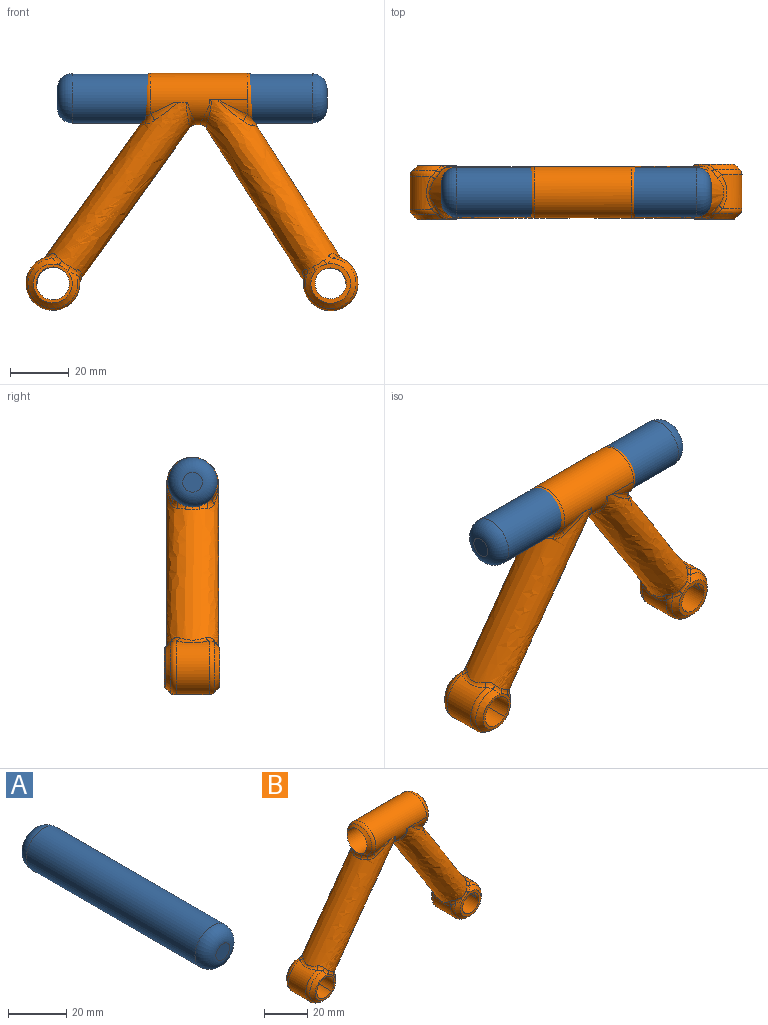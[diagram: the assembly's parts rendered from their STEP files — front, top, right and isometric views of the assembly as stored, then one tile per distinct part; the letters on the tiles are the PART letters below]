
ASSEMBLY  parts=2 mates=1
PART A: 5 faces, bbox 16.9x92.2x16.9 mm
  f0: cylinder r=8.44mm len=82.04mm, axis (0,1,0), area 4351.7mm2, adj f3,f4
  f1: plane 6.72x6.72mm, normal (0,-1,0), area 35.5mm2, adj f4
  f2: plane 6.72x6.72mm, normal (0,1,0), area 35.5mm2, adj f3
  f3: torus R=3.36mm, axis (0,-1,0), area 330.7mm2, adj f0,f2
  f4: torus R=3.36mm, axis (0,-1,0), area 330.7mm2, adj f0,f1
PART B: 77 faces, bbox 115.2x35.7x82.8 mm
  f0: bspline ~61.06x60.5mm, area -3132mm2, adj f1,f14,f15,f16,f17,f18,f61,f62
  f1: bspline ~3.72x3.66mm, area 5.3mm2, adj f0,f2,f14,f75
  f2: cone r=6.64mm half-angle=45deg, axis (0,1,0), area 103.2mm2, adj f1,f3,f13,f15
  f3: plane 13.37x13.37mm, normal (0,1,0), area 39.1mm2, adj f2,f4,f12,f14
  f4: cylinder r=5.63mm len=18.46mm, axis (0,1,0), area 294.9mm2, adj f3,f5,f9,f10,f11,f12
  f5: plane 13.4x13.4mm, normal (0,-1,0), area 39.1mm2, adj f4,f6,f12,f71
  f6: cone r=9.18mm half-angle=45deg, axis (0,-1,0), area 102.3mm2, adj f5,f7,f70,f72
  f7: torus R=6.64mm, axis (0,1,0), area 86.6mm2, adj f6,f8,f73,f76
  f8: cylinder r=9.18mm len=18.37mm, axis (0,1,0), area 458.9mm2, adj f7,f13,f17,f74
  f9: bspline ~62.14x61.9mm, area 2.3mm2, adj f4,f10,f12
  f10: plane 14.44x0.21mm, normal (0,0,1), area 2.9mm2, adj f4,f9,f11,f12
  f11: bspline ~62.14x61.9mm, area 2.3mm2, adj f4,f10,f12
  f12: cylinder r=5.54mm len=18.46mm, axis (0,-1,0), area 357.5mm2, adj f3,f4,f5,f9,f10,f11
  f13: torus R=6.64mm, axis (0,-1,0), area 86.9mm2, adj f2,f8,f16,f75
  f14: bspline ~3.96x3.44mm, area 5.7mm2, adj f0,f1,f3,f15
  f15: bspline ~4.19x3.14mm, area 5.4mm2, adj f0,f2,f14,f16
  f16: bspline ~3.67x3.62mm, area 6.2mm2, adj f0,f13,f15,f17
  f17: bspline ~12.35x3.69mm, area 19.5mm2, adj f0,f8,f16,f76
  f18: plane 4.62x0.29mm, normal (0,0,-1), area 0.4mm2, adj f0,f19,f61,f69
  f19: cylinder r=8.79mm len=33.15mm, axis (-1,0,0), area 1126.3mm2, adj f18,f20,f55,f56,f57,f58,f59,f60
  f20: torus R=6.25mm, axis (-1,0,0), area 78.1mm2, adj f19,f21,f62,f66
  f21: cone r=8.79mm half-angle=45deg, axis (1,0,0), area 82mm2, adj f20,f22,f54,f63,f65
  f22: cylinder r=6.45mm len=40.34mm, axis (1,0,0), area 1635mm2, adj f21,f23,f53,f54
  f23: plane 6.63x0.95mm, normal (-1,0,0), area 0.2mm2, adj f22,f24,f53
  f24: bspline ~3.25x2.13mm, area 3.5mm2, adj f23,f25,f28,f52
  f25: bspline ~5.66x3.16mm, area 14.1mm2, adj f24,f26,f28,f53
  f26: bspline ~4.31x4.23mm, area 10.1mm2, adj f25,f27,f28,f58
  f27: bspline ~11.26x8.45mm, area 18.7mm2, adj f26,f28,f59,f60
  f28: bspline ~61.2x56.79mm, area 3044.4mm2, adj f24,f25,f26,f27,f29,f42,f43,f44
  f29: bspline ~3.79x3.75mm, area 6.1mm2, adj f28,f30,f42,f51
  f30: torus R=6.78mm, axis (0,-1,0), area 87.2mm2, adj f29,f31,f41,f48
  f31: cylinder r=9.32mm len=18.64mm, axis (0,1,0), area 475.5mm2, adj f30,f32,f42,f47
  f32: torus R=6.78mm, axis (0,1,0), area 89.2mm2, adj f31,f33,f43,f45
  f33: cone r=9.32mm half-angle=45deg, axis (0,-1,0), area 107.2mm2, adj f32,f34,f44
  f34: plane 13.56x13.56mm, normal (0,-1,0), area 55.2mm2, adj f33,f35,f40
  f35: cylinder r=5.24mm len=18.79mm, axis (0,-1,0), area 378.4mm2, adj f34,f36,f37,f38,f39,f40
  f36: plane 13.7x13.7mm, normal (0,1,0), area 55.2mm2, adj f35,f40,f41,f50
  f37: bspline ~62.76x57.82mm, area 1.9mm2, adj f35,f38,f40
  f38: plane 14.79x0.21mm, normal (0,0,1), area 3mm2, adj f35,f37,f39,f40
  f39: bspline ~62.76x57.82mm, area 1.9mm2, adj f35,f38,f40
  f40: cylinder r=5.31mm len=18.79mm, axis (0,1,0), area 249mm2, adj f34,f35,f36,f37,f38,f39
  f41: cone r=6.78mm half-angle=45deg, axis (0,1,0), area 103.3mm2, adj f30,f36,f49,f51
  f42: bspline ~13.05x4.05mm, area 19.8mm2, adj f28,f29,f31,f43
  f43: bspline ~4.16x4.01mm, area 6.8mm2, adj f28,f32,f42,f44
  f44: bspline ~9.08x6.53mm, area 16.6mm2, adj f28,f33,f43,f45
  f45: bspline ~4.62x4.09mm, area 6.7mm2, adj f28,f32,f44,f47
  f46: bspline ~4.41x4.4mm, area 10.1mm2, adj f28,f52,f57,f58
  f47: bspline ~13.31x3.55mm, area 18.9mm2, adj f28,f31,f45,f48
  f48: bspline ~3.8x3.54mm, area 5.9mm2, adj f28,f30,f47,f49
  f49: bspline ~4.16x3.84mm, area 5mm2, adj f28,f41,f48,f50
  f50: bspline ~5.84x4.65mm, area 6.1mm2, adj f28,f36,f49,f51
  f51: bspline ~3.57x2.77mm, area 5.1mm2, adj f28,f29,f41,f50
  f52: bspline ~5.12x3.16mm, area 14.1mm2, adj f24,f28,f46,f53
  f53: cone r=6.25mm half-angle=45deg, axis (-1,0,0), area 100.3mm2, adj f22,f23,f25,f52,f58
  f54: plane 6.74x1.06mm, normal (1,0,0), area 0.2mm2, adj f21,f22,f64
  f55: bspline ~17.63x10.2mm, area 47.5mm2, adj f19,f28,f56,f60
  f56: plane 3.34x0.15mm, normal (0,0,-1), area 0.2mm2, adj f19,f28,f55,f57
  f57: bspline ~11.08x8.22mm, area 18.7mm2, adj f19,f28,f46,f56
  f58: torus R=6.25mm, axis (1,0,0), area 80.1mm2, adj f19,f26,f46,f53,f59
  f59: cylinder r=8.79mm len=9.72mm, axis (-1,0,0), area 26.1mm2, adj f19,f27,f58
  f60: plane 3.33x0.15mm, normal (0,0,-1), area 0.2mm2, adj f19,f27,f28,f55
  f61: bspline ~10.72x7.52mm, area 17.1mm2, adj f0,f18,f19,f62
  f62: bspline ~4.28x4.13mm, area 9.4mm2, adj f0,f20,f61,f63
  f63: bspline ~4.88x3.22mm, area 10mm2, adj f0,f21,f62,f64
  f64: bspline ~4.84x3.16mm, area 13.9mm2, adj f0,f54,f63,f65
  f65: bspline ~4.48x3.2mm, area 10mm2, adj f0,f21,f64,f66
  f66: bspline ~3.97x3.89mm, area 9.4mm2, adj f0,f20,f65,f67
  f67: bspline ~10.64x7.48mm, area 17.1mm2, adj f0,f19,f66,f68
  f68: plane 4.62x0.29mm, normal (0,0,-1), area 0.4mm2, adj f0,f19,f67,f69
  f69: bspline ~17.54x8.92mm, area 44.4mm2, adj f0,f18,f19,f68
  f70: bspline ~3.91x2.88mm, area 5.2mm2, adj f0,f6,f71,f76
  f71: bspline ~4.32x3.67mm, area 5.8mm2, adj f0,f5,f70,f72
  f72: bspline ~3.91x3.91mm, area 5mm2, adj f0,f6,f71,f73
  f73: bspline ~3.75x3.54mm, area 5.9mm2, adj f0,f7,f72,f74
  f74: bspline ~12.68x3.59mm, area 18.3mm2, adj f0,f8,f73,f75
  f75: bspline ~3.94x3.72mm, area 6mm2, adj f0,f1,f13,f74
  f76: bspline ~4.39x4.27mm, area 6.1mm2, adj f0,f7,f17,f70
PLACE A rot(axis=(0,0,1),90deg) t=(-52.92,119.38,148.71)mm
PLACE B t=(0.75,119.38,85.42)mm
MATE cylindrical A.f0 <-> B.f22  axis (-1,0,0) through (-6.82,119.38,148.71)mm
